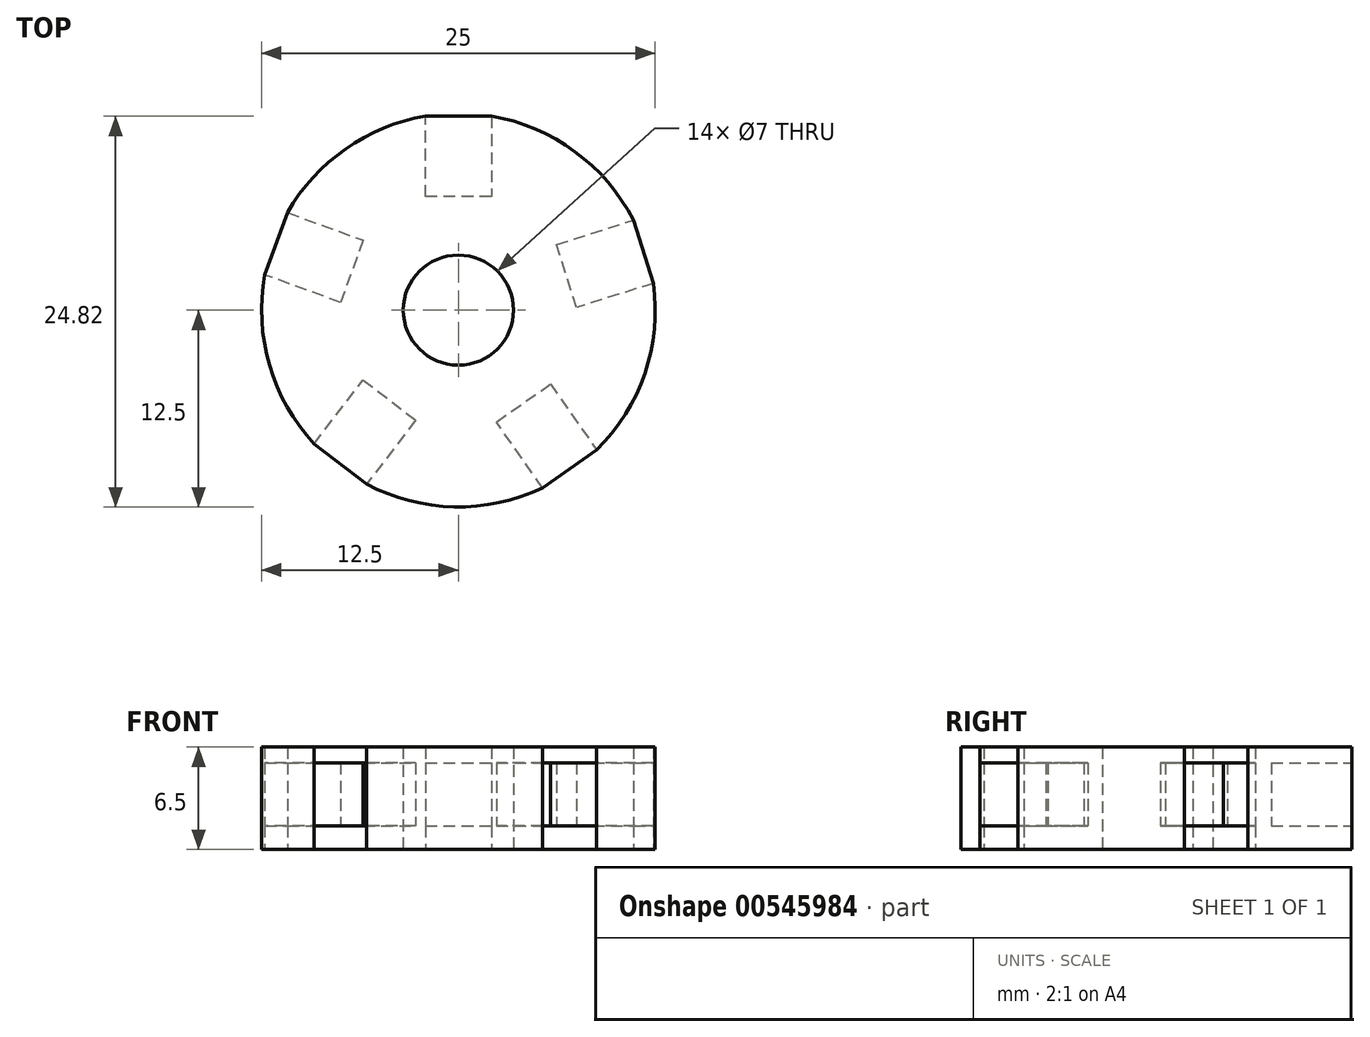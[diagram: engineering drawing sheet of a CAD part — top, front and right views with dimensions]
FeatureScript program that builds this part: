
annotation { "Feature Type Name" : "Feature", "Feature Type Description" : "" }
export const myFeature = defineFeature(function(context is Context, id is Id, definition is map)
    precondition{}
    {
        {
            var Q0;
            Q0=qCreatedBy(makeId("Top.planeOp"),FACE);
            var sketch = newSketch(context, id + "F0", { "sketchPlane" : qUnion([Q0])});
            skCircle(sketch, "E0", {"center": v(0, 0) * mm, "radius": 3.5 * mm});
            skCircle(sketch, "E1", {"center": v(0, 0) * mm, "radius": 7.5 * mm});
            skCircle(sketch, "E2", {"center": v(0, 0) * mm, "radius": 12.5 * mm});
            skLineSegment(sketch, "E3", {"start": v(-2.1, 12.32) * mm, "end": v(2.1, 12.32) * mm});
            skLineSegment(sketch, "E4", {"start": v(2.1, 12.32) * mm, "end": v(2.1, 7.2) * mm});
            skLineSegment(sketch, "E5", {"start": v(2.1, 7.2) * mm, "end": v(-2.1, 7.2) * mm});
            skLineSegment(sketch, "E6", {"start": v(-2.1, 7.2) * mm, "end": v(-2.1, 12.32) * mm});
            skPoint(sketch, "E7", {"position": v(0, 12.32) * mm});
            skLineSegment(sketch, "E8.1.0", {"start": v(6.24, 4.17) * mm, "end": v(11.12, 5.7) * mm});
            skLineSegment(sketch, "E8.1.1", {"start": v(12.38, 1.7) * mm, "end": v(7.5, 0.16) * mm});
            skLineSegment(sketch, "E8.1.2", {"start": v(11.12, 5.7) * mm, "end": v(12.38, 1.7) * mm});
            skLineSegment(sketch, "E8.1.3", {"start": v(7.5, 0.16) * mm, "end": v(6.24, 4.17) * mm});
            skLineSegment(sketch, "E8.2.0", {"start": v(5.85, -4.7) * mm, "end": v(8.79, -8.89) * mm});
            skLineSegment(sketch, "E8.2.1", {"start": v(5.35, -11.3) * mm, "end": v(2.4, -7.1) * mm});
            skLineSegment(sketch, "E8.2.2", {"start": v(8.79, -8.89) * mm, "end": v(5.35, -11.3) * mm});
            skLineSegment(sketch, "E8.2.3", {"start": v(2.4, -7.1) * mm, "end": v(5.85, -4.7) * mm});
            skLineSegment(sketch, "E8.3.0", {"start": v(-2.72, -7) * mm, "end": v(-5.84, -11.05) * mm});
            skLineSegment(sketch, "E8.3.1", {"start": v(-9.17, -8.5) * mm, "end": v(-6.05, -4.43) * mm});
            skLineSegment(sketch, "E8.3.2", {"start": v(-5.84, -11.05) * mm, "end": v(-9.17, -8.5) * mm});
            skLineSegment(sketch, "E8.3.3", {"start": v(-6.05, -4.43) * mm, "end": v(-2.72, -7) * mm});
            skLineSegment(sketch, "E8.4.0", {"start": v(-7.48, 0.49) * mm, "end": v(-12.3, 2.24) * mm});
            skLineSegment(sketch, "E8.4.1", {"start": v(-10.86, 6.19) * mm, "end": v(-6.05, 4.44) * mm});
            skLineSegment(sketch, "E8.4.2", {"start": v(-12.3, 2.24) * mm, "end": v(-10.86, 6.19) * mm});
            skLineSegment(sketch, "E8.4.3", {"start": v(-6.05, 4.44) * mm, "end": v(-7.48, 0.49) * mm});
            skLineSegment(sketch, "E8.anchor1", {"start": v(0, 0) * mm, "end": v(-2.1, 7.2) * mm, "construction": true});
            skLineSegment(sketch, "E8.anchor2", {"start": v(0, 0) * mm, "end": v(-7.48, 0.49) * mm, "construction": true});
            skSolve(sketch);
        }
        {
            var Q0;
            {var subQ0=sQuery(id+"F0.wireOp",EDGE,"E8.3.1");Q0=makeQuery(id+"F0.imprint","IMPRINT",FACE,{"disambiguationData":[TD([[makeQuery(id+"F0.imprint","IMPRINT",EDGE,{"derivedFrom":subQ0}),1.0]])]});}
            var Q1;
            {var subQ0=sQuery(id+"F0.wireOp",EDGE,"E6");Q1=makeQuery(id+"F0.imprint","IMPRINT",FACE,{"disambiguationData":[TD([[makeQuery(id+"F0.imprint","IMPRINT",EDGE,{"derivedFrom":subQ0}),1.0]])]});}
            var Q2;
            {var subQ0=sQuery(id+"F0.wireOp",EDGE,"E4");Q2=makeQuery(id+"F0.imprint","IMPRINT",FACE,{"disambiguationData":[TD([[makeQuery(id+"F0.imprint","IMPRINT",EDGE,{"derivedFrom":subQ0}),1.0]])]});}
            var Q3;
            {var subQ0=sQuery(id+"F0.wireOp",EDGE,"E8.1.1");Q3=makeQuery(id+"F0.imprint","IMPRINT",FACE,{"disambiguationData":[TD([[makeQuery(id+"F0.imprint","IMPRINT",EDGE,{"derivedFrom":subQ0}),1.0]])]});}
            var Q4;
            {var subQ0=sQuery(id+"F0.wireOp",EDGE,"E8.2.1");Q4=makeQuery(id+"F0.imprint","IMPRINT",FACE,{"disambiguationData":[TD([[makeQuery(id+"F0.imprint","IMPRINT",EDGE,{"derivedFrom":subQ0}),1.0]])]});}
            var Q5;
            {var subQ1=sQuery(id+"F0.wireOp",EDGE,"E8.4.0");Q5=makeQuery(id+"F0.imprint","IMPRINT",FACE,{"disambiguationData":[TD([[makeQuery(id+"F0.imprint","IMPRINT",EDGE,{"derivedFrom":subQ1}),-1.0]])]});}
            var Q6;
            {var subQ1=sQuery(id+"F0.wireOp",EDGE,"E8.2.0");Q6=makeQuery(id+"F0.imprint","IMPRINT",FACE,{"disambiguationData":[TD([[makeQuery(id+"F0.imprint","IMPRINT",EDGE,{"derivedFrom":subQ1}),-1.0]])]});}
            var Q7;
            {var subQ1=sQuery(id+"F0.wireOp",EDGE,"E8.3.0");Q7=makeQuery(id+"F0.imprint","IMPRINT",FACE,{"disambiguationData":[TD([[makeQuery(id+"F0.imprint","IMPRINT",EDGE,{"derivedFrom":subQ1}),-1.0]])]});}
            var Q8;
            {var subQ0=sQuery(id+"F0.wireOp",EDGE,"E8.4.3");Q8=makeQuery(id+"F0.imprint","IMPRINT",FACE,{"disambiguationData":[TD([[makeQuery(id+"F0.imprint","IMPRINT",EDGE,{"derivedFrom":subQ0}),-1.0]])]});}
            var Q9;
            Q9=makeQuery(id+"F0.imprint","IMPRINT",FACE,{"disambiguationData":[TD([[makeQuery(id+"F0.imprint","IMPRINT",EDGE,{"derivedFrom":sQuery(id+"F0.wireOp",EDGE,"E3")}),-1.0]])]});
            var Q10;
            {var subQ0=sQuery(id+"F0.wireOp",EDGE,"E5");Q10=makeQuery(id+"F0.imprint","IMPRINT",FACE,{"disambiguationData":[TD([[makeQuery(id+"F0.imprint","IMPRINT",EDGE,{"derivedFrom":subQ0}),-1.0]])]});}
            var Q11;
            {var subQ0=sQuery(id+"F0.wireOp",EDGE,"E8.3.3");Q11=makeQuery(id+"F0.imprint","IMPRINT",FACE,{"disambiguationData":[TD([[makeQuery(id+"F0.imprint","IMPRINT",EDGE,{"derivedFrom":subQ0}),-1.0]])]});}
            var Q12;
            Q12=makeQuery(id+"F0.imprint","IMPRINT",FACE,{"disambiguationData":[TD([[makeQuery(id+"F0.imprint","IMPRINT",EDGE,{"derivedFrom":sQuery(id+"F0.wireOp",EDGE,"E0")}),-1.0]])]});
            var Q13;
            {var subQ0=sQuery(id+"F0.wireOp",EDGE,"E8.2.3");Q13=makeQuery(id+"F0.imprint","IMPRINT",FACE,{"disambiguationData":[TD([[makeQuery(id+"F0.imprint","IMPRINT",EDGE,{"derivedFrom":subQ0}),-1.0]])]});}
            var Q14;
            {var subQ0=sQuery(id+"F0.wireOp",EDGE,"E8.1.3");Q14=makeQuery(id+"F0.imprint","IMPRINT",FACE,{"disambiguationData":[TD([[makeQuery(id+"F0.imprint","IMPRINT",EDGE,{"derivedFrom":subQ0}),-1.0]])]});}
            var Q15;
            {var subQ1=sQuery(id+"F0.wireOp",EDGE,"E8.1.0");Q15=makeQuery(id+"F0.imprint","IMPRINT",FACE,{"disambiguationData":[TD([[makeQuery(id+"F0.imprint","IMPRINT",EDGE,{"derivedFrom":subQ1}),-1.0]])]});}
            extrude(context, id + "F1", {"entities" : qUnion([Q0, Q1, Q2, Q3, Q4, Q5, Q6, Q7, Q8, Q9, Q10, Q11, Q12, Q13, Q14, Q15]), "depth" : 6.5 * mm, "offsetDistance" : 25 * mm});
        }
        {
            var Q0;
            {var subQ1=sQuery(id+"F0.wireOp",EDGE,"E8.3.0");Q0=makeQuery(id+"F0.imprint","IMPRINT",FACE,{"disambiguationData":[TD([[makeQuery(id+"F0.imprint","IMPRINT",EDGE,{"derivedFrom":subQ1}),-1.0]])]});}
            var Q1;
            {var subQ0=sQuery(id+"F0.wireOp",EDGE,"E8.3.3");Q1=makeQuery(id+"F0.imprint","IMPRINT",FACE,{"disambiguationData":[TD([[makeQuery(id+"F0.imprint","IMPRINT",EDGE,{"derivedFrom":subQ0}),-1.0]])]});}
            var Q2;
            {var subQ1=sQuery(id+"F0.wireOp",EDGE,"E8.4.0");Q2=makeQuery(id+"F0.imprint","IMPRINT",FACE,{"disambiguationData":[TD([[makeQuery(id+"F0.imprint","IMPRINT",EDGE,{"derivedFrom":subQ1}),-1.0]])]});}
            var Q3;
            {var subQ0=sQuery(id+"F0.wireOp",EDGE,"E8.4.3");Q3=makeQuery(id+"F0.imprint","IMPRINT",FACE,{"disambiguationData":[TD([[makeQuery(id+"F0.imprint","IMPRINT",EDGE,{"derivedFrom":subQ0}),-1.0]])]});}
            var Q4;
            Q4=makeQuery(id+"F0.imprint","IMPRINT",FACE,{"disambiguationData":[TD([[makeQuery(id+"F0.imprint","IMPRINT",EDGE,{"derivedFrom":sQuery(id+"F0.wireOp",EDGE,"E3")}),-1.0]])]});
            var Q5;
            {var subQ0=sQuery(id+"F0.wireOp",EDGE,"E5");Q5=makeQuery(id+"F0.imprint","IMPRINT",FACE,{"disambiguationData":[TD([[makeQuery(id+"F0.imprint","IMPRINT",EDGE,{"derivedFrom":subQ0}),-1.0]])]});}
            var Q6;
            {var subQ1=sQuery(id+"F0.wireOp",EDGE,"E8.1.0");Q6=makeQuery(id+"F0.imprint","IMPRINT",FACE,{"disambiguationData":[TD([[makeQuery(id+"F0.imprint","IMPRINT",EDGE,{"derivedFrom":subQ1}),-1.0]])]});}
            var Q7;
            {var subQ0=sQuery(id+"F0.wireOp",EDGE,"E8.1.3");Q7=makeQuery(id+"F0.imprint","IMPRINT",FACE,{"disambiguationData":[TD([[makeQuery(id+"F0.imprint","IMPRINT",EDGE,{"derivedFrom":subQ0}),-1.0]])]});}
            var Q8;
            {var subQ1=sQuery(id+"F0.wireOp",EDGE,"E8.2.0");Q8=makeQuery(id+"F0.imprint","IMPRINT",FACE,{"disambiguationData":[TD([[makeQuery(id+"F0.imprint","IMPRINT",EDGE,{"derivedFrom":subQ1}),-1.0]])]});}
            var Q9;
            {var subQ0=sQuery(id+"F0.wireOp",EDGE,"E8.2.3");Q9=makeQuery(id+"F0.imprint","IMPRINT",FACE,{"disambiguationData":[TD([[makeQuery(id+"F0.imprint","IMPRINT",EDGE,{"derivedFrom":subQ0}),-1.0]])]});}
            extrude(context, id + "F2", {"entities" : qUnion([Q0, Q1, Q2, Q3, Q4, Q5, Q6, Q7, Q8, Q9]), "operationType" : NewBodyOperationType.REMOVE, "depth" : 5.5 * mm, "offsetDistance" : 25 * mm, "hasSecondDirection" : true, "secondDirectionOppositeDirection" : false, "secondDirectionDepth" : 1.5 * mm});
        }
    });
